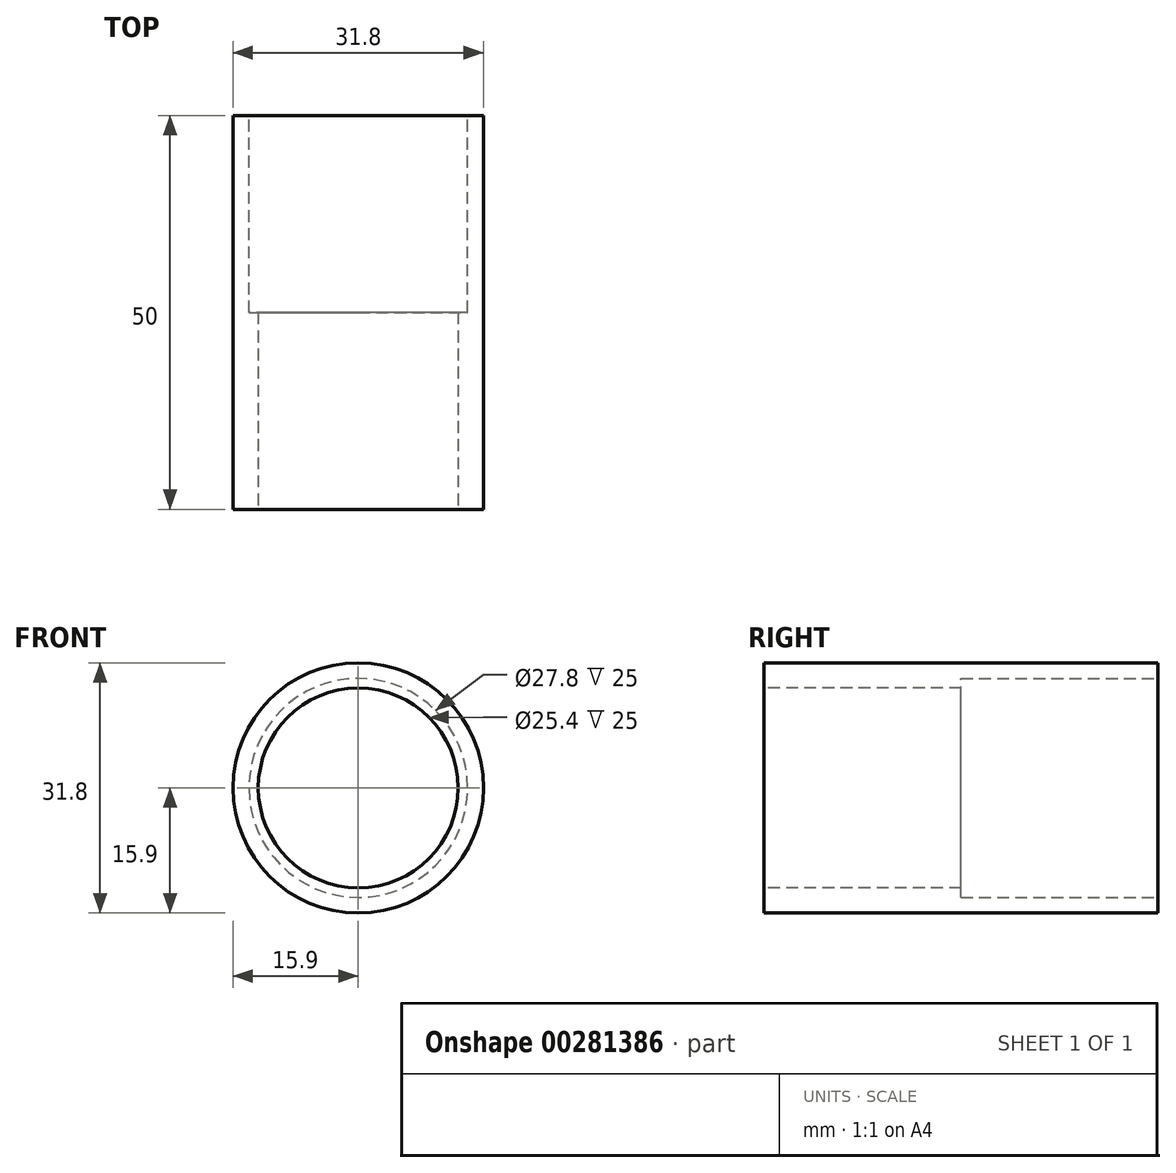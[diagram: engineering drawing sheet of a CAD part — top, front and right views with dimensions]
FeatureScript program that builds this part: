
annotation { "Feature Type Name" : "Feature", "Feature Type Description" : "" }
export const myFeature = defineFeature(function(context is Context, id is Id, definition is map)
    precondition{}
    {
        {
            var Q0;
            Q0=qCreatedBy(makeId("Front.planeOp"),FACE);
            var sketch = newSketch(context, id + "F0", { "sketchPlane" : qUnion([Q0])});
            skCircle(sketch, "E0", {"center": v(0, 0) * mm, "radius": 13.9 * mm});
            skCircle(sketch, "E1", {"center": v(0, 0) * mm, "radius": 15.9 * mm});
            skSolve(sketch);
        }
        {
            var Q0;
            Q0=makeQuery(id+"F0.imprint","IMPRINT",FACE,{"disambiguationData":[TD([[makeQuery(id+"F0.imprint","IMPRINT",EDGE,{"derivedFrom":sQuery(id+"F0.wireOp",EDGE,"E0")}),-1.0]])]});
            extrude(context, id + "F1", {"entities" : qUnion([Q0]), "depth" : 50 * mm});
        }
        {
            var Q0;
            Q0=makeQuery(id+"F1.opExtrude","CAP_FACE",FACE,{"disambiguationData":[OSD([sQuery(id+"F0.wireOp",EDGE,"E0"),sQuery(id+"F0.wireOp",EDGE,"E1")])],"isStart":false});
            var sketch = newSketch(context, id + "F2", { "sketchPlane" : qUnion([Q0])});
            skCircle(sketch, "E2", {"center": v(0, 0) * mm, "radius": 12.7 * mm});
            skCircle(sketch, "E3.0", {"center": v(0, 0) * mm, "radius": 13.9 * mm});
            skSolve(sketch);
        }
        {
            var Q0;
            Q0=makeQuery(id+"F2.imprint","IMPRINT",FACE,{"disambiguationData":[TD([[makeQuery(id+"F2.imprint","IMPRINT",EDGE,{"derivedFrom":sQuery(id+"F2.wireOp",EDGE,"E2")}),-1.0]])]});
            extrude(context, id + "F3", {"entities" : qUnion([Q0]), "operationType" : NewBodyOperationType.ADD, "oppositeDirection" : true, "depth" : 25 * mm});
        }
    });
